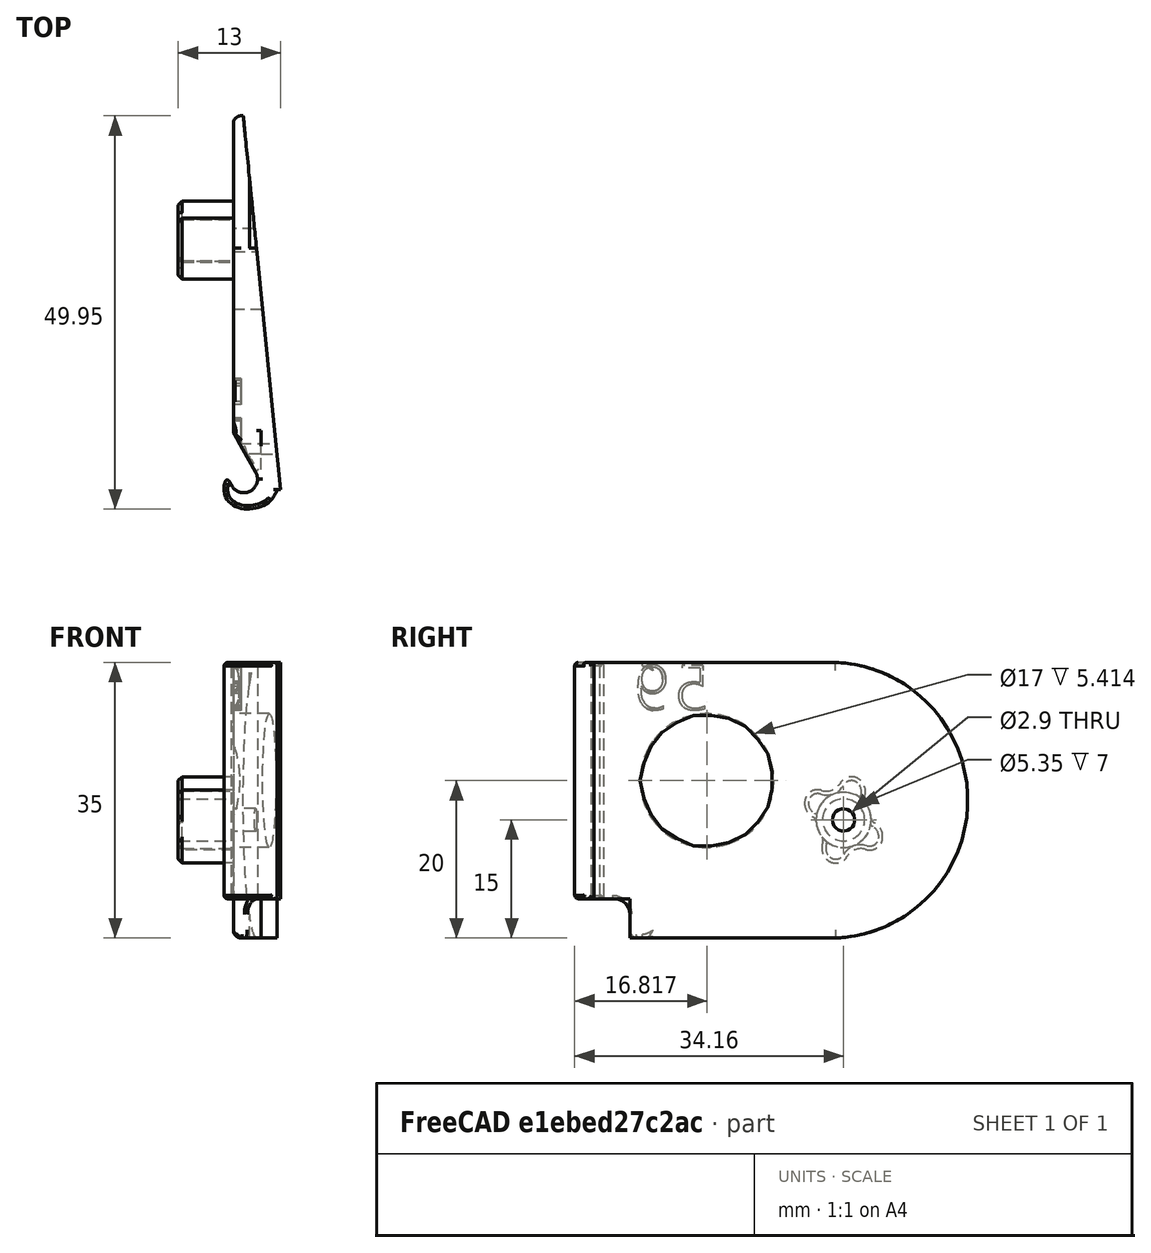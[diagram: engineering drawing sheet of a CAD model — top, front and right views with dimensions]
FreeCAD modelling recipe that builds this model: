
FCSTD DOCUMENT  (FreeCAD 0.18R)
Label: hinge-left-159deg-angled
License: All rights reserved
LicenseURL: http://en.wikipedia.org/wiki/All_rights_reserved
objects: App::FeaturePython×4, Part::FeaturePython×2, Part::Part2DObjectPython×1, Part::Extrusion×1, Part::Cut×1
note: 5 computed .brp shape members not serialized (recipe doc carries the construction recipe); baked Part::Feature solids carry a one-line shape summary decoded from their .brp

FEATURE [Part::FeaturePython] bracket_left_001  label="bracket-left_001"  # a2plus imported part (geometry in sourceFile) (typed FeaturePython)
  a2p_Version = V0.1
  fixedPosition = true
  objectType = a2pPart
  sourceFile = ./parts/bracket-left.fcstd
  subassemblyImport = false
  timeLastImport = 1.60454e+09
  updateColors = true
FEATURE [Part::FeaturePython] pillar_base_001  label="pillar-base_001"  # a2plus imported part (geometry in sourceFile) (typed FeaturePython)
  Placement = pos=(0.000608724,-0.981981,1.95002) rot=(-1,0,0;0.069988rad)
  a2p_Version = V0.1
  fixedPosition = false
  objectType = a2pPart
  sourceFile = ./parts/pillar-base.fcstd
  subassemblyImport = false
  timeLastImport = 1.60452e+09
  updateColors = true
FEATURE [Part::Part2DObjectPython] ShapeString  # Draft 2D object (typed FeaturePython)
  FontFile = <path>
  Placement = pos=(1.61,10.5,29) rot=(0.57735,-0.57735,-0.57735;2.0944rad)
  Size = 6
  String = 59
  Tracking = 0
FEATURE [Part::Extrusion] Extrude
  Base = -> ShapeString
  Dir = (-1,0,0)
  DirMode = 2
  FaceMakerClass = Part::FaceMakerBullseye
  LengthFwd = 2
  LengthRev = 0
  Solid = false
  Symmetric = false
FEATURE [App::FeaturePython] axisCoincident_001  label="axisCoincident_001__bracket-left_001"  # a2plus constraint (typed FeaturePython)
  Object1 = pillar_base_001
  Object2 = bracket_left_001
  ParentTreeObject = -> pillar_base_001
  SubElement1 = Face17
  SubElement2 = Face39
  Suppressed = false
  Type = axial
  directionConstraint = 1
  lockRotation = false
FEATURE [App::FeaturePython] axisCoincident_001_mirror  label="axisCoincident_001__pillar-base_001"  # a2plus constraint (typed FeaturePython)
  Object1 = pillar_base_001
  Object2 = bracket_left_001
  ParentTreeObject = -> bracket_left_001
  SubElement1 = Face17
  SubElement2 = Face39
  Suppressed = false
  Type = axial
  directionConstraint = 1
  lockRotation = false
FEATURE [App::FeaturePython] planeCoincident_001  label="planeCoincident_001__bracket-left_001"  # a2plus constraint (typed FeaturePython)
  Object1 = pillar_base_001
  Object2 = bracket_left_001
  ParentTreeObject = -> pillar_base_001
  SubElement1 = Face1
  SubElement2 = Face65
  Suppressed = false
  Type = plane
  directionConstraint = 0
  offset = 0
FEATURE [App::FeaturePython] planeCoincident_001_mirror  label="planeCoincident_001__pillar-base_001"  # a2plus constraint (typed FeaturePython)
  Object1 = pillar_base_001
  Object2 = bracket_left_001
  ParentTreeObject = -> bracket_left_001
  SubElement1 = Face1
  SubElement2 = Face65
  Suppressed = false
  Type = plane
  directionConstraint = 0
  offset = 0
FEATURE [Part::Cut] Cut
  Base = -> bracket_left_001
  Tool = -> Extrude
note: 1 file-system path scrubbed to <path> (originals preserved in the JSON sidecar)
